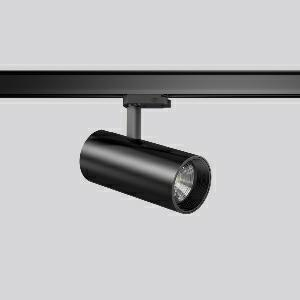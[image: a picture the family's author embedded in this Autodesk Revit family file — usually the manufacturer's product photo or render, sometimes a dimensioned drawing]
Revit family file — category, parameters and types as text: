
# Revit family: deecos_s_mini_742199_003_1_76_fc57
name_source: partatom
category: Lighting Fixtures
units: mm (PartAtom-declared; Revit-internal decimal feet)

## family parameters
Cut with Voids When Loaded = No
Host = Face
Light Source = No
Part Type = Normal
Room Calculation Point = No
Round Connector Dimension = Use Diameter
Shared = No

## types (1)
- DEECOS S mini (1 x LED Modul 940, 2250 lm, 4000)
    Apparent Load = 20 VA
    Approval mark = CE
    CIE Flux Codes = 96 100 100 100 100
    Color Rendering = 92
    Color Temperature = 4000
    Default Elevation = 1800 mm
    Description = Series: DEECOS S mini
LED surface-mounted projector in modern design with no visible cooling ribs. Housing: die-cast aluminium, powder-coated. Rotation range: 356°. Swivel range: 90°. Black plastic ring and recessed LED to prevent glare from the side. Optical assembly with lens made of plastic (polycarbonate) for the best homogeneous light distribution - can be changed without tools. Best colour rendering index Ra>90. With adapter for RZB 3-circuit DALI tracks. Suitable for Track on ceiling, Wall track. High quality converter without flickering and stroboscopic effect. The following accessories can be mounted without use of tools: interchangeable lenses, decorative glasses, honeycomb louvre, clear and frosted diffusers, white interchangeable plastic ring. 
Colour: deep black, matt (RAL 9005)
Diameter: 87 mm
Height: 214 mm
Lamp: LED
Socket: without socket
Colour temperature: 4000K
Colour rendering index (CRI): 92
System power: 20 W
Rated luminous flux: 2250 lm
Luminous efficiency: 113 lm/W
Control gear: Converter, dimmable, DALI
Protection class: I
Type of protection: IP 20
    Height = 214 mm
    Lamp = 1 x LED Modul 940
    Lamp Light Flux = 2250 lm
    Lamp count = 1
    Length = 87 mm
    Lifetime = 50000 h
    Luminous efficacy = 113 lm/W
    Manufacturer = RZB
    ModVariant = No
    Model = 742199.003.1.76
    Mounting Place = Ceiling
    Mounting Type = Rail mounted
    Number of Poles = 1
    OnlyDefault = Yes
    Power Factor = 1
    Product Name = DEECOS S mini
    Product group = Track mounted projectors
    ProductGroupID = 301
    Protection Class = Protection class I
    Protection Degree = IP 20
    RLX_Detail_Level = 1
    RLX_Emergency_Light_Flux = 0 lm
    RLX_Emergency_Type = 0
    RLX_Emergency_Type_DB = No
    RlxData = <blob elided: 39249 chars, md5=d9e2f93a>
    Socket = socket
    Standby Power = 0 W
    System Light Flux = 2250 lm
    System Power = 20 W
    Type Comments = Product without accessories
    Type Image = 741930.003.jpg
    URL = http://relux.com
    VarID = ---
    Voltage = 230 V
    Voltage Range = 220-240 V
    Weight = 0.00 kg
    Width = 0 mm  [stored 0 ft]

note: [stored X ft] marks values corroborated as IEEE doubles in the binary element streams (Revit-internal decimal feet)

## geometry (parser evidence)
native form markers: Blend x4, Sweep x12
no freeform markers — native parametric forms only
